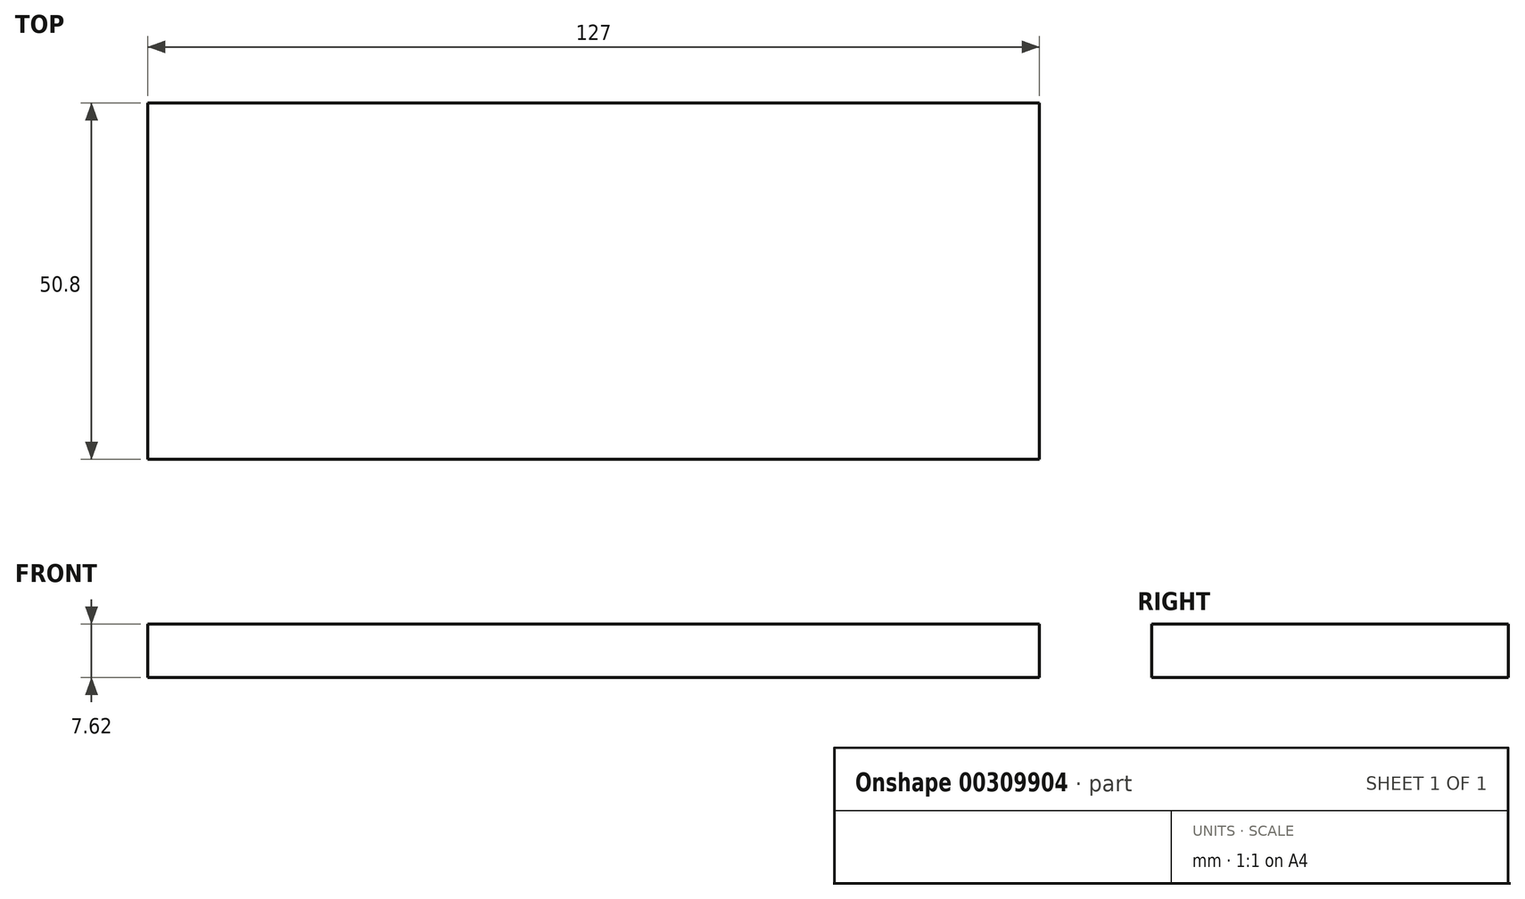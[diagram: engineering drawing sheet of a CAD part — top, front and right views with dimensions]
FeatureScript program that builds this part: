
annotation { "Feature Type Name" : "Feature", "Feature Type Description" : "" }
export const myFeature = defineFeature(function(context is Context, id is Id, definition is map)
    precondition{}
    {
        {
            var Q0;
            Q0=qCreatedBy(makeId("Top.planeOp"),FACE);
            var sketch = newSketch(context, id + "F0", { "sketchPlane" : qUnion([Q0])});
            skLineSegment(sketch, "E0.bottom", {"start": v(-65.14, 38) * mm, "end": v(61.86, 38) * mm});
            skLineSegment(sketch, "E0.top", {"start": v(-65.14, -12.8) * mm, "end": v(61.86, -12.8) * mm});
            skLineSegment(sketch, "E0.left", {"start": v(-65.14, 38) * mm, "end": v(-65.14, -12.8) * mm});
            skLineSegment(sketch, "E0.right", {"start": v(61.86, 38) * mm, "end": v(61.86, -12.8) * mm});
            skSolve(sketch);
        }
        {
            var Q0;
            Q0 = qSketchRegion(id + "F0", true);
            var Q1;
            Q1=makeQuery(id+"F0.imprint","IMPRINT",FACE,{"disambiguationData":[TD([[makeQuery(id+"F0.imprint","IMPRINT",EDGE,{"derivedFrom":sQuery(id+"F0.wireOp",EDGE,"E0.bottom")}),-1.0]])]});
            extrude(context, id + "F1", {"entities" : qUnion([Q0, Q1]), "depth" : 7.62 * mm});
        }
    });
